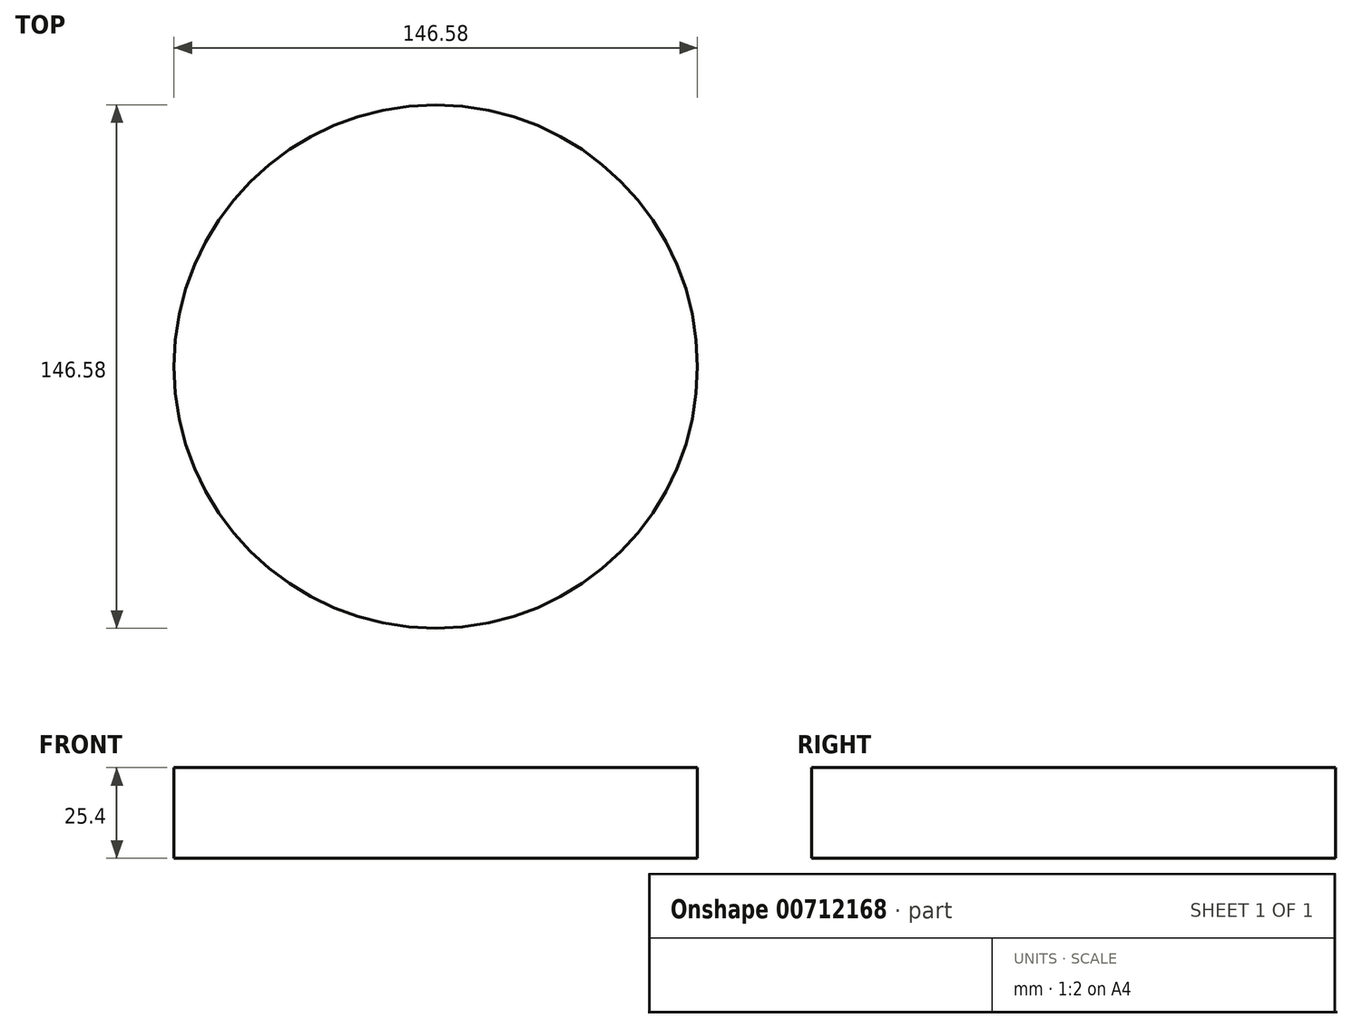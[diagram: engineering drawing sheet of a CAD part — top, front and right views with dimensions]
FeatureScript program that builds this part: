
annotation { "Feature Type Name" : "Feature", "Feature Type Description" : "" }
export const myFeature = defineFeature(function(context is Context, id is Id, definition is map)
    precondition{}
    {
        {
            var Q0;
            Q0=qCreatedBy(makeId("Top.planeOp"),FACE);
            var sketch = newSketch(context, id + "F0", { "sketchPlane" : qUnion([Q0])});
            skCircle(sketch, "E0", {"center": v(0, 0) * mm, "radius": 73.29 * mm});
            skCircle(sketch, "E1", {"center": v(0, 46.81) * mm, "radius": 10.45 * mm});
            skCircle(sketch, "E2", {"center": v(48.98, -0.85) * mm, "radius": 11.62 * mm});
            skCircle(sketch, "E3", {"center": v(-49.69, 0) * mm, "radius": 12.15 * mm});
            skCircle(sketch, "E4", {"center": v(0, -41.63) * mm, "radius": 12.1 * mm});
            skSolve(sketch);
        }
        {
            var Q0;
            Q0=sQuery(id+"F0.wireOp",EDGE,"E0");
            extrude(context, id + "F1", {"bodyType" : ToolBodyType.SURFACE, "surfaceEntities" : qUnion([Q0]), "depth" : 25.4 * mm, "offsetDistance" : 25.4 * mm});
        }
    });
